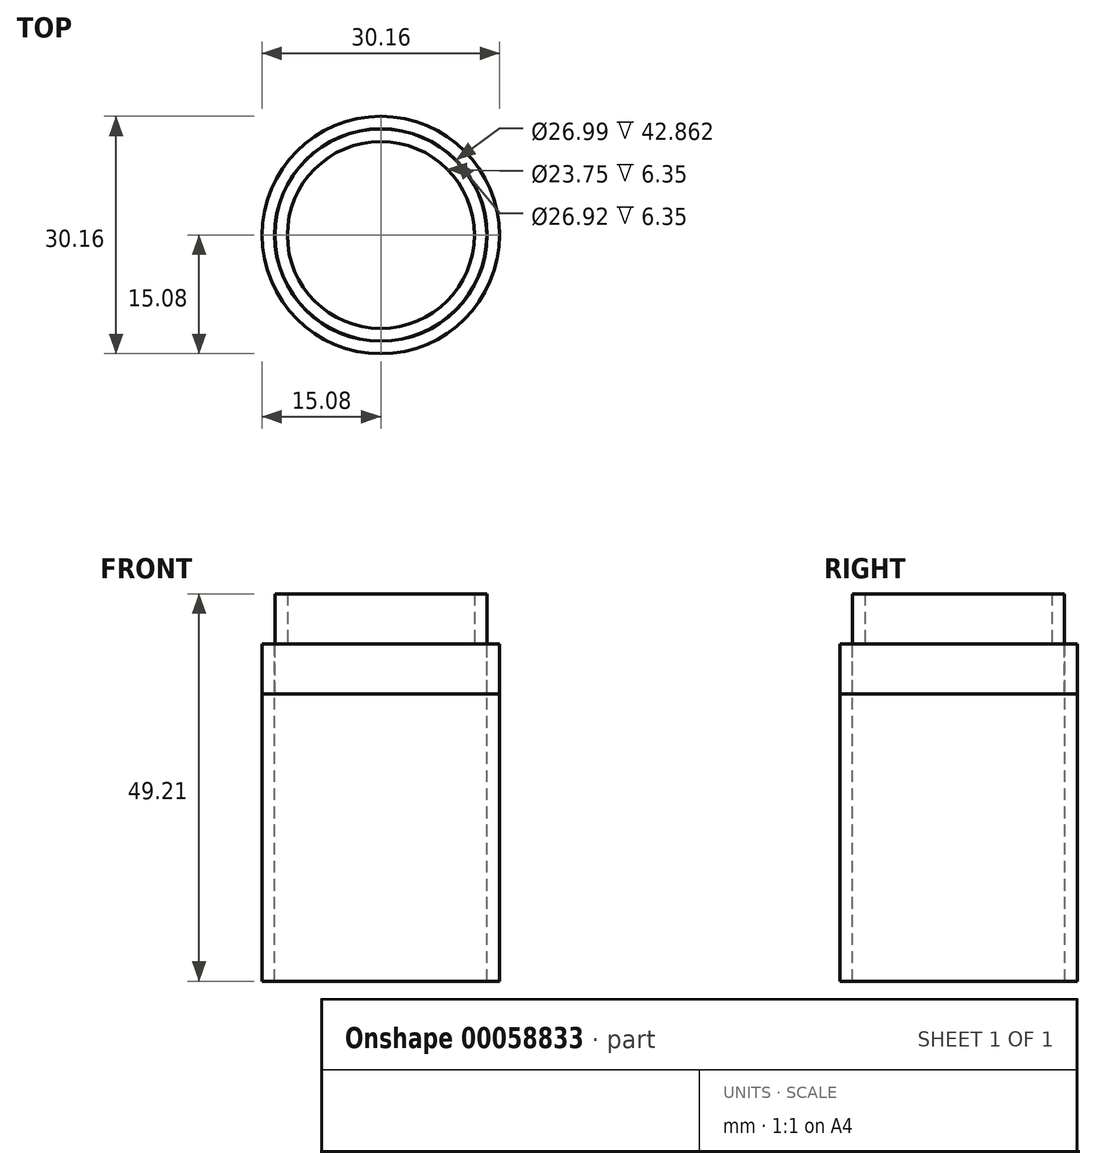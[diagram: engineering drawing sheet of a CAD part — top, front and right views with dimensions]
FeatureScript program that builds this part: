
annotation { "Feature Type Name" : "Feature", "Feature Type Description" : "" }
export const myFeature = defineFeature(function(context is Context, id is Id, definition is map)
    precondition{}
    {
        {
            var Q0;
            Q0=qCreatedBy(makeId("Top.planeOp"),FACE);
            var sketch = newSketch(context, id + "F0", { "sketchPlane" : qUnion([Q0])});
            skCircle(sketch, "E0", {"center": v(0, 0) * mm, "radius": 11.87 * mm});
            skCircle(sketch, "E1", {"center": v(0, 0) * mm, "radius": 13.46 * mm});
            skSolve(sketch);
        }
        {
            var Q0;
            Q0 = qSketchRegion(id + "F0", true);
            extrude(context, id + "F1", {"entities" : qUnion([Q0]), "depth" : 6.35 * mm});
        }
        {
            var Q0;
            Q0=qCreatedBy(makeId("Top.planeOp"),FACE);
            var sketch = newSketch(context, id + "F2", { "sketchPlane" : qUnion([Q0])});
            skCircle(sketch, "E2", {"center": v(0, 0) * mm, "radius": 13.5 * mm});
            skCircle(sketch, "E3", {"center": v(0, 0) * mm, "radius": 15.08 * mm});
            skSolve(sketch);
        }
        {
            var Q0;
            Q0 = qSketchRegion(id + "F2", true);
            extrude(context, id + "F3", {"entities" : qUnion([Q0]), "operationType" : NewBodyOperationType.ADD, "oppositeDirection" : true, "depth" : 42.86 * mm});
        }
        {
            var Q0;
            Q0=qCreatedBy(makeId("Top.planeOp"),FACE);
            var sketch = newSketch(context, id + "F4", { "sketchPlane" : qUnion([Q0])});
            skCircle(sketch, "E4", {"center": v(0, 0) * mm, "radius": 13.46 * mm});
            skCircle(sketch, "E5", {"center": v(0, 0) * mm, "radius": 15.08 * mm});
            skSolve(sketch);
        }
        {
            var Q0;
            Q0 = qSketchRegion(id + "F4", true);
            extrude(context, id + "F5", {"entities" : qUnion([Q0]), "oppositeDirection" : true, "depth" : 6.35 * mm});
        }
    });
